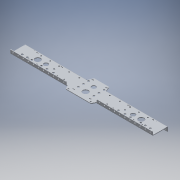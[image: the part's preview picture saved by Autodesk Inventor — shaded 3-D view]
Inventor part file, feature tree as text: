
AUTODESK INVENTOR PART (.ipt)
format: ipt  version: 2017 (Build 210142000, 142)  size: 353,792 bytes
history: native  units: in
note: dims shown in document units (in); Inventor stores cm internally (conversion verified against a paired STEP export)
features: extrude x1, sketch x1, other x1
ambient origin geometry x8: Origin, YZ Plane, XZ Plane, XY Plane, X Axis, Y Axis, Z Axis, Center Point
bodies: Solid1 (feature_tree)
feature tree (3):
  extrude  "Extrusion1"  Depth=2.0in
  sketch  "Sketch1"  dims[d0=2.0in d1=2.0in d2=0.0in d3=0.0in]
  other  "Cut-Extrude16"
